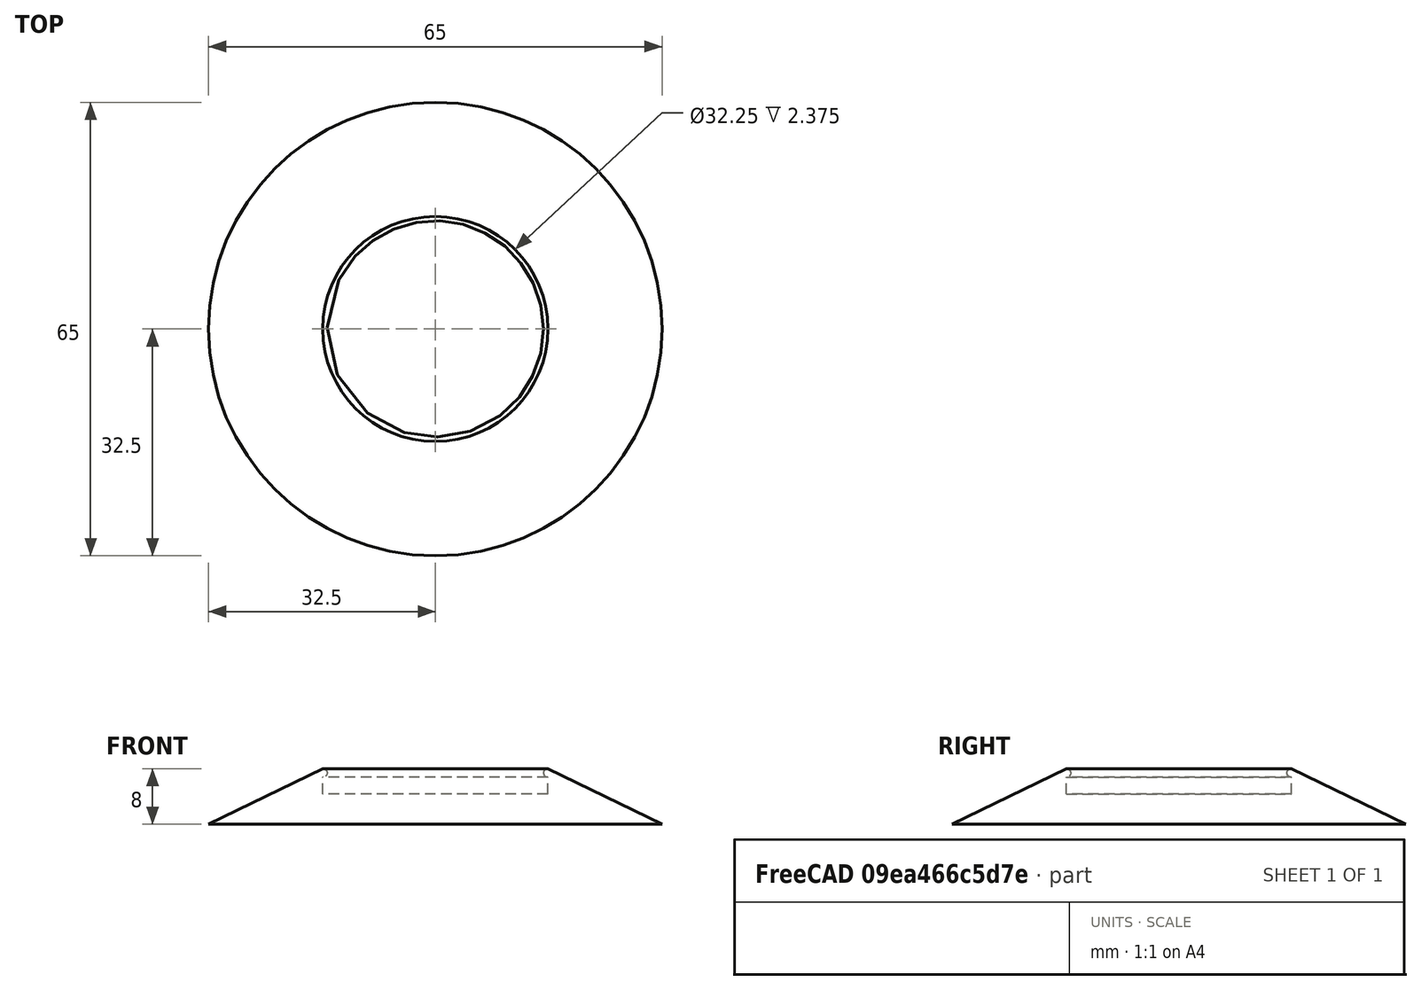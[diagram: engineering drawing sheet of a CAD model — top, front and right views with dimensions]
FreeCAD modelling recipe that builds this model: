
FCSTD DOCUMENT  (FreeCAD 0.20R27319 (Git))
Label: Measuring Code Base
License: All rights reserved
LicenseURL: http://en.wikipedia.org/wiki/All_rights_reserved
objects: Sketcher::SketchObject×1, PartDesign::Revolution×1, PartDesign::Body×1
note: 4 computed .brp shape members not serialized (recipe doc carries the construction recipe); baked Part::Feature solids carry a one-line shape summary decoded from their .brp

FEATURE [Sketcher::SketchObject] Sketch
  FullyConstrained = true
  MapMode = 5
  Placement = pos=(0,0,0) rot=(1,0,0;1.5708rad)
  Support = -> [XZ_Plane]
  expr: Constraints[20] = 31 / 2
  expr: Constraints[7] = 32.25mm / 2
  sketch-geometry (7):
    g0: LineSegment StartX=32.5 StartY=0 StartZ=0 EndX=16.125 EndY=8 EndZ=0
    g1: LineSegment StartX=0 StartY=0 StartZ=0 EndX=0 EndY=4.375 EndZ=0
    g2: LineSegment StartX=0 StartY=4.375 StartZ=0 EndX=16.125 EndY=4.375 EndZ=0
    g3: LineSegment StartX=16.125 StartY=4.375 StartZ=0 EndX=16.125 EndY=6.75 EndZ=0
    g4: ArcOfCircle CenterX=16.125 CenterY=7.375 CenterZ=0 NormalX=0 NormalY=0 NormalZ=1 AngleXU=0 Radius=0.625 StartAngle=1.5708 EndAngle=4.71239
    g5: LineSegment StartX=0 StartY=0 StartZ=0 EndX=32.5 EndY=0 EndZ=0
    g6: LineSegment StartX=0 StartY=7.375 StartZ=0 EndX=15.5 EndY=7.375 EndZ=0
  constraints (22):
    c: PointOnObject(g1,g-2)
    c: Coincident(g1,g2)
    c: Horizontal(g2)
    c: Coincident(g3,g2)
    c: Vertical(g3)
    c: Coincident(g4,g0)
    c: Coincident(g4,g3)
    c: DistanceX(g2,g2) = 16.125
    c: Vertical(g4,g0)
    c: Vertical(g0,g3)
    c: DistanceY(g-1,g0) = 8
    c: DistanceX(g-1,g0) = 32.5
    c: Coincident(g5,g1)
    c: Coincident(g5,g0)
    c: Horizontal(g5)
    c: Coincident(g1,g-1)
    c: PointOnObject(g6,g-2)
    c: PointOnObject(g6,g4)
    c: Horizontal(g6)
    c: Perpendicular(g4,g6)
    c: DistanceX(g6,g6) = 15.5
    c: DistanceY(g2,g4) = 3
FEATURE [PartDesign::Revolution] Revolution
  Angle = 360
  Axis = (0,2e-16,1)
  Base = (0,0,0)
  Placement = pos=(0,0,0) rot=(1,0,0;1.5708rad)
  Profile = -> Sketch
  ReferenceAxis = -> Sketch [V_Axis]
  Reversed = true
FEATURE [PartDesign::Body] Body
  Group = -> [Sketch,Revolution]
  Origin = -> Origin
  Tip = -> Revolution
